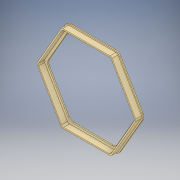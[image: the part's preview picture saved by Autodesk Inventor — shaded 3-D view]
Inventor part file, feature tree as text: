
AUTODESK INVENTOR PART (.ipt)
format: ipt  version: 2019 (Build 230136000, 136)  size: 186,368 bytes
history: native  units: mm
features: extrude x3, sketch x3, fillet x2, projected_geometry x2
ambient origin geometry x8: Origin, YZ Plane, XZ Plane, XY Plane, X Axis, Y Axis, Z Axis, Center Point
bodies: Solid1 (feature_tree)
feature tree (10):
  extrude  "Extrusion1"  Depth=2.0mm TaperAngle=0.0deg
  extrude  "Extrusion5"  Depth=2.0mm
  extrude  "Extrusion6"  Depth=4.0mm
  fillet  "Fillet1"  Radius=7.0mm
  fillet  "Fillet2"  Radius=10.0mm
  sketch  "Sketch1"  dims[d0=150.0mm d1=2.0mm d2=0.0mm]
  sketch  "Sketch5"  dims[d15=2.0mm d16=2.0mm]
  projected_geometry  "Projected Loop4"
  sketch  "Sketch7"  dims[d17=10.0mm d18=0.0mm d19=4.0mm d20=7.0mm d21=0.0mm d22=10.0mm d23=4.0mm d24=10.0mm]
  projected_geometry  "Projected Loop6"
